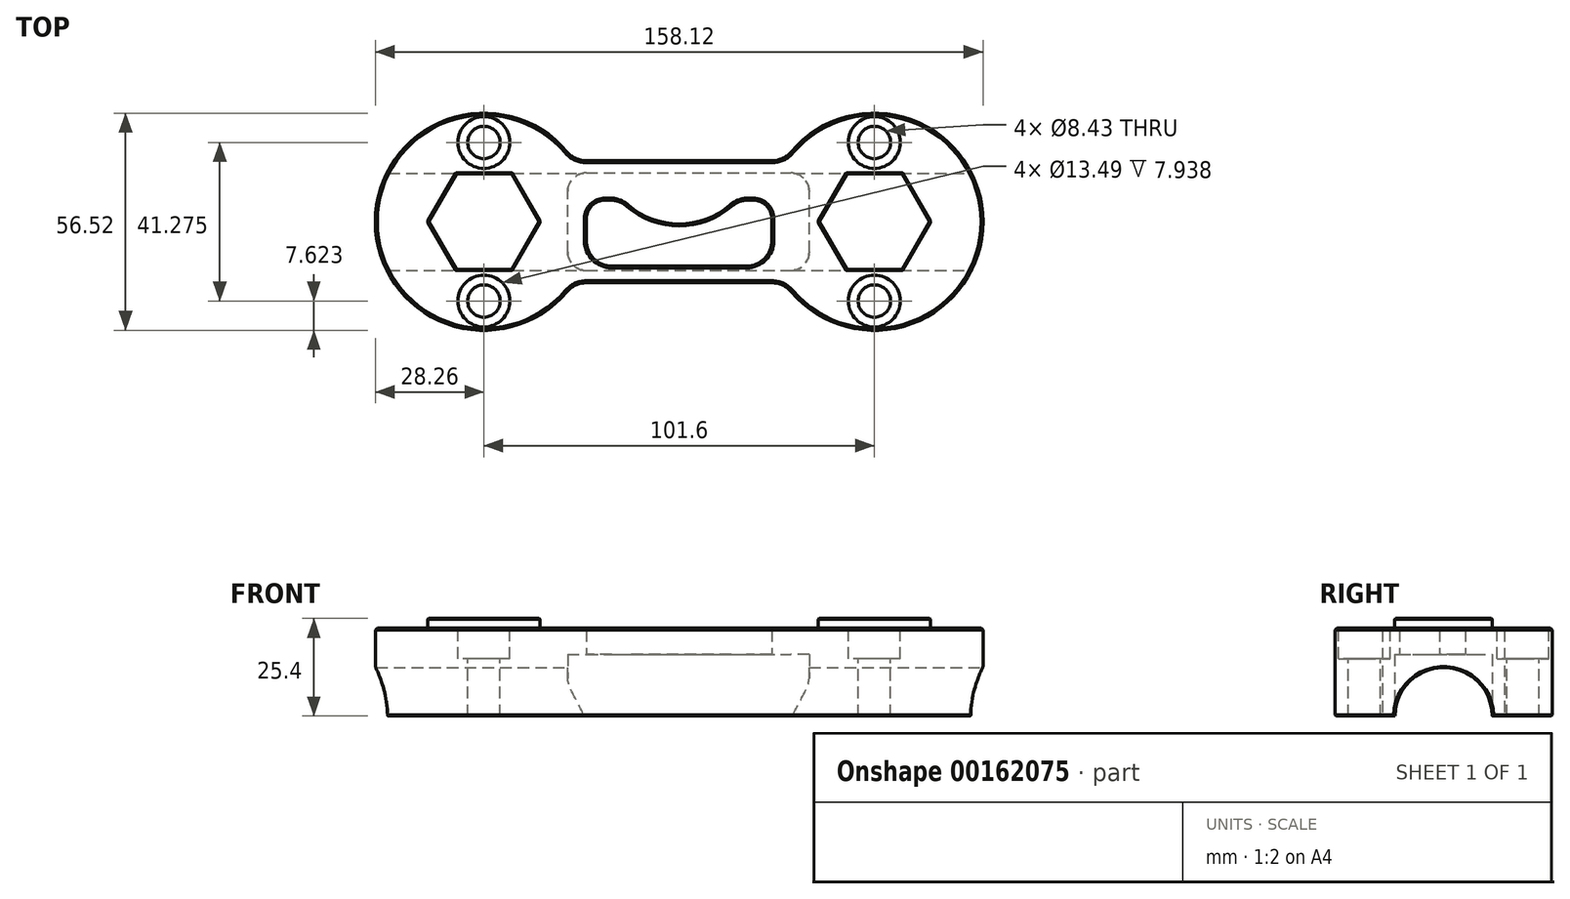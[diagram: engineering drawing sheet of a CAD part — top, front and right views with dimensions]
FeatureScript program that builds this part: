
annotation { "Feature Type Name" : "Feature", "Feature Type Description" : "" }
export const myFeature = defineFeature(function(context is Context, id is Id, definition is map)
    precondition{}
    {
        {
            var Q0;
            Q0=qCreatedBy(makeId("Top.planeOp"),FACE);
            var sketch = newSketch(context, id + "F0", { "sketchPlane" : qUnion([Q0])});
            skPoint(sketch, "E0", {"position": v(-50.8, 0) * mm});
            skPoint(sketch, "E1", {"position": v(50.8, 0) * mm});
            skArc(sketch, "E2", {"start": v(-29.2, 18.22) * mm, "mid": v(-79.06, 0) * mm, "end": v(-29.2, -18.22) * mm});
            skArc(sketch, "E3", {"start": v(29.2, -18.22) * mm, "mid": v(79.06, 0) * mm, "end": v(29.2, 18.22) * mm});
            skLineSegment(sketch, "E4", {"start": v(-24.15, 15.88) * mm, "end": v(24.15, 15.88) * mm});
            skLineSegment(sketch, "E5", {"start": v(-24.15, -15.87) * mm, "end": v(24.15, -15.87) * mm});
            skPoint(sketch, "E6.orphan", {"position": v(-45.55, -15.87) * mm});
            skPoint(sketch, "E7.orphan", {"position": v(-45.55, 15.88) * mm});
            skPoint(sketch, "E8.orphan", {"position": v(44.18, 15.88) * mm});
            skPoint(sketch, "E9.orphan", {"position": v(44.18, -15.87) * mm});
            skPoint(sketch, "E10.visualSharp", {"position": v(-27.42, 15.88) * mm});
            skArc(sketch, "E10.filletArc", {"start": v(-29.2, 18.22) * mm, "mid": v(-26.94, 16.5) * mm, "end": v(-24.15, 15.88) * mm});
            skPoint(sketch, "E11.visualSharp", {"position": v(27.42, 15.88) * mm});
            skArc(sketch, "E11.filletArc", {"start": v(24.15, 15.88) * mm, "mid": v(26.94, 16.5) * mm, "end": v(29.2, 18.22) * mm});
            skPoint(sketch, "E12.visualSharp", {"position": v(-27.42, -15.88) * mm});
            skArc(sketch, "E12.filletArc", {"start": v(-24.15, -15.88) * mm, "mid": v(-26.94, -16.5) * mm, "end": v(-29.2, -18.22) * mm});
            skPoint(sketch, "E13.visualSharp", {"position": v(27.42, -15.87) * mm});
            skArc(sketch, "E13.filletArc", {"start": v(29.2, -18.22) * mm, "mid": v(26.94, -16.5) * mm, "end": v(24.15, -15.88) * mm});
            skSolve(sketch);
        }
        {
            var Q0;
            Q0 = qSketchRegion(id + "F0", true);
            extrude(context, id + "F1", {"entities" : qUnion([Q0]), "depth" : 22.86 * mm});
        }
        {
            var Q0;
            Q0=qCreatedBy(makeId("Right.planeOp"),FACE);
            var sketch = newSketch(context, id + "F2", { "sketchPlane" : qUnion([Q0])});
            skCircle(sketch, "E14", {"center": v(0, 0) * mm, "radius": 12.64 * mm});
            skSolve(sketch);
        }
        {
            var Q0;
            Q0 = qSketchRegion(id + "F2", true);
            extrude(context, id + "F3", {"entities" : qUnion([Q0]), "operationType" : NewBodyOperationType.REMOVE, "endBound" : BoundingType.THROUGH_ALL, "oppositeDirection" : true, "depth" : 25.4 * mm, "hasSecondDirection" : true, "secondDirectionBound" : SecondDirectionBoundingType.THROUGH_ALL, "secondDirectionOppositeDirection" : false, "secondDirectionDepth" : 25.4 * mm});
        }
        {
            var Q0;
            Q0=qCreatedBy(makeId("Top.planeOp"),FACE);
            var sketch = newSketch(context, id + "F4", { "sketchPlane" : qUnion([Q0])});
            skPoint(sketch, "E15", {"position": v(-50.73, 0.06) * mm});
            skPoint(sketch, "E16", {"position": v(50.87, 0.06) * mm});
            skLineSegment(sketch, "E17.bottom", {"start": v(-24.18, -12.7) * mm, "end": v(29.02, -12.7) * mm});
            skLineSegment(sketch, "E17.top", {"start": v(-24.18, 12.7) * mm, "end": v(29.02, 12.7) * mm});
            skLineSegment(sketch, "E17.left", {"start": v(-29, -7.87) * mm, "end": v(-29, 7.87) * mm});
            skLineSegment(sketch, "E17.right", {"start": v(33.84, -7.87) * mm, "end": v(33.84, 7.87) * mm});
            skPoint(sketch, "E18.visualSharp", {"position": v(-29, -12.7) * mm});
            skArc(sketch, "E18.filletArc", {"start": v(-29, -7.87) * mm, "mid": v(-27.6, -11.29) * mm, "end": v(-24.18, -12.7) * mm});
            skPoint(sketch, "E19.visualSharp", {"position": v(-29, 12.7) * mm});
            skArc(sketch, "E19.filletArc", {"start": v(-24.18, 12.7) * mm, "mid": v(-27.6, 11.29) * mm, "end": v(-29, 7.87) * mm});
            skPoint(sketch, "E20.visualSharp", {"position": v(33.84, 12.7) * mm});
            skArc(sketch, "E20.filletArc", {"start": v(33.84, 7.87) * mm, "mid": v(32.43, 11.29) * mm, "end": v(29.02, 12.7) * mm});
            skPoint(sketch, "E21.visualSharp", {"position": v(33.84, -12.7) * mm});
            skArc(sketch, "E21.filletArc", {"start": v(29.02, -12.7) * mm, "mid": v(32.43, -11.29) * mm, "end": v(33.84, -7.87) * mm});
            skSolve(sketch);
        }
        {
            var Q0;
            Q0 = qSketchRegion(id + "F4", true);
            extrude(context, id + "F5", {"entities" : qUnion([Q0]), "operationType" : NewBodyOperationType.REMOVE, "depth" : 16 * mm});
        }
        {
            var Q0;
            Q0=makeQuery(id+"F5.boolean.opBoolean","COPY",FACE,{"derivedFrom":makeQuery(id+"F5.opExtrude","CAP_FACE",FACE,{"disambiguationData":[OSD([sQuery(id+"F4.wireOp",EDGE,"E17.bottom"),sQuery(id+"F4.wireOp",EDGE,"E17.top"),sQuery(id+"F4.wireOp",EDGE,"E17.left"),sQuery(id+"F4.wireOp",EDGE,"E17.right")])],"isStart":false})});
            var sketch = newSketch(context, id + "F6", { "sketchPlane" : qUnion([Q0])});
            skPoint(sketch, "E22.middle", {"position": v(0, 0) * mm});
            skLineSegment(sketch, "E23.bottom", {"start": v(-17.53, 11.52) * mm, "end": v(17.53, 11.52) * mm});
            skLineSegment(sketch, "E23.top", {"start": v(-19.3, -5.63) * mm, "end": v(-17.92, -5.63) * mm});
            skLineSegment(sketch, "E23.left", {"start": v(-24.13, 4.91) * mm, "end": v(-24.13, -0.8) * mm});
            skLineSegment(sketch, "E23.right", {"start": v(24.13, 4.91) * mm, "end": v(24.13, -0.8) * mm});
            skPoint(sketch, "E23.middle", {"position": v(0, 2.94) * mm});
            skPoint(sketch, "E24", {"position": v(-15.24, -5.63) * mm});
            skPoint(sketch, "E25", {"position": v(15.24, -5.63) * mm});
            skArc(sketch, "E26", {"start": v(13.57, -4) * mm, "mid": v(0, 1.1) * mm, "end": v(-13.57, -4) * mm});
            skLineSegment(sketch, "E27.trimOffspring", {"start": v(17.92, -5.63) * mm, "end": v(19.3, -5.63) * mm});
            skPoint(sketch, "E28.visualSharp", {"position": v(-24.13, 11.52) * mm});
            skArc(sketch, "E28.filletArc", {"start": v(-17.53, 11.52) * mm, "mid": v(-22.2, 9.58) * mm, "end": v(-24.13, 4.91) * mm});
            skPoint(sketch, "E29.visualSharp", {"position": v(24.13, 11.52) * mm});
            skArc(sketch, "E29.filletArc", {"start": v(24.13, 4.91) * mm, "mid": v(22.2, 9.58) * mm, "end": v(17.53, 11.52) * mm});
            skPoint(sketch, "E30.visualSharp", {"position": v(-24.13, -5.63) * mm});
            skArc(sketch, "E30.filletArc", {"start": v(-24.13, -0.8) * mm, "mid": v(-22.72, -4.21) * mm, "end": v(-19.3, -5.63) * mm});
            skArc(sketch, "E31.filletArc", {"start": v(-17.92, -5.63) * mm, "mid": v(-15.6, -5.2) * mm, "end": v(-13.57, -4) * mm});
            skPoint(sketch, "E32.visualSharp", {"position": v(24.13, -5.63) * mm});
            skArc(sketch, "E32.filletArc", {"start": v(19.3, -5.63) * mm, "mid": v(22.72, -4.21) * mm, "end": v(24.13, -0.8) * mm});
            skArc(sketch, "E33.filletArc", {"start": v(13.57, -4) * mm, "mid": v(15.6, -5.2) * mm, "end": v(17.92, -5.63) * mm});
            skSolve(sketch);
        }
        {
            var Q0;
            Q0 = qSketchRegion(id + "F6", true);
            extrude(context, id + "F7", {"entities" : qUnion([Q0]), "operationType" : NewBodyOperationType.REMOVE, "oppositeDirection" : true, "depth" : 25.4 * mm});
        }
        {
            var Q0;
            Q0=makeQuery(id+"F1.opExtrude","CAP_FACE",FACE,{"disambiguationData":[OSD([sQuery(id+"F0.wireOp",EDGE,"E2"),sQuery(id+"F0.wireOp",EDGE,"E3"),sQuery(id+"F0.wireOp",EDGE,"E4"),sQuery(id+"F0.wireOp",EDGE,"E5"),sQuery(id+"F0.wireOp",EDGE,"E10.filletArc"),sQuery(id+"F0.wireOp",EDGE,"E11.filletArc"),sQuery(id+"F0.wireOp",EDGE,"E12.filletArc"),sQuery(id+"F0.wireOp",EDGE,"E13.filletArc")])],"isStart":false});
            var sketch = newSketch(context, id + "F8", { "sketchPlane" : qUnion([Q0])});
            skCircle(sketch, "E34", {"center": v(-50.8, 0) * mm, "radius": 12.7 * mm});
            skCircle(sketch, "E35", {"center": v(50.8, 0) * mm, "radius": 12.7 * mm});
            skCircle(sketch, "E36.cCircle", {"center": v(-50.8, 0) * mm, "radius": 12.7 * mm, "construction": true});
            skLineSegment(sketch, "E36.0", {"start": v(-58.13, 12.7) * mm, "end": v(-43.47, 12.7) * mm});
            skLineSegment(sketch, "E36.1", {"start": v(-43.47, 12.7) * mm, "end": v(-36.14, 0) * mm});
            skLineSegment(sketch, "E36.2", {"start": v(-36.14, 0) * mm, "end": v(-43.47, -12.7) * mm});
            skLineSegment(sketch, "E36.3", {"start": v(-43.47, -12.7) * mm, "end": v(-58.13, -12.7) * mm});
            skLineSegment(sketch, "E36.4", {"start": v(-58.13, -12.7) * mm, "end": v(-65.46, 0) * mm});
            skLineSegment(sketch, "E36.5", {"start": v(-65.46, 0) * mm, "end": v(-58.13, 12.7) * mm});
            skPoint(sketch, "E36.0.midPoint", {"position": v(-50.8, 12.7) * mm});
            skCircle(sketch, "E37.cCircle", {"center": v(50.8, 0) * mm, "radius": 12.7 * mm, "construction": true});
            skLineSegment(sketch, "E37.0", {"start": v(43.47, 12.7) * mm, "end": v(58.13, 12.7) * mm});
            skLineSegment(sketch, "E37.1", {"start": v(58.13, 12.7) * mm, "end": v(65.46, 0) * mm});
            skLineSegment(sketch, "E37.2", {"start": v(65.46, 0) * mm, "end": v(58.13, -12.7) * mm});
            skLineSegment(sketch, "E37.3", {"start": v(58.13, -12.7) * mm, "end": v(43.47, -12.7) * mm});
            skLineSegment(sketch, "E37.4", {"start": v(43.47, -12.7) * mm, "end": v(36.14, 0) * mm});
            skLineSegment(sketch, "E37.5", {"start": v(36.14, 0) * mm, "end": v(43.47, 12.7) * mm});
            skPoint(sketch, "E37.0.midPoint", {"position": v(50.8, 12.7) * mm});
            skSolve(sketch);
        }
        {
            var Q0;
            Q0 = qSketchRegion(id + "F8", true);
            extrude(context, id + "F9", {"entities" : qUnion([Q0]), "operationType" : NewBodyOperationType.ADD, "depth" : 2.54 * mm});
        }
        {
            var Q0;
            Q0=makeQuery(id+"F1.opExtrude","CAP_FACE",FACE,{"disambiguationData":[OSD([sQuery(id+"F0.wireOp",EDGE,"E2"),sQuery(id+"F0.wireOp",EDGE,"E3"),sQuery(id+"F0.wireOp",EDGE,"E4"),sQuery(id+"F0.wireOp",EDGE,"E5"),sQuery(id+"F0.wireOp",EDGE,"E10.filletArc"),sQuery(id+"F0.wireOp",EDGE,"E11.filletArc"),sQuery(id+"F0.wireOp",EDGE,"E12.filletArc"),sQuery(id+"F0.wireOp",EDGE,"E13.filletArc")])],"isStart":false});
            var sketch = newSketch(context, id + "F10", { "sketchPlane" : qUnion([Q0])});
            skPoint(sketch, "E38.startSnap0", {"position": v(-50.8, 12.7) * mm});
            skPoint(sketch, "E39.startSnap0", {"position": v(50.8, 12.7) * mm});
            skPoint(sketch, "E39.endSnap0", {"position": v(50.8, -12.7) * mm});
            skPoint(sketch, "E40", {"position": v(-50.8, 20.64) * mm});
            skPoint(sketch, "E41", {"position": v(-50.8, -20.64) * mm});
            skPoint(sketch, "E42", {"position": v(50.8, 20.64) * mm});
            skPoint(sketch, "E43", {"position": v(50.8, -20.64) * mm});
            skSolve(sketch);
        }
        {
            var Q0;
            Q0=sQuery(id+"F10.wireOp",VERTEX,"E40");
            var Q1;
            Q1=sQuery(id+"F10.wireOp",VERTEX,"E41");
            var Q2;
            Q2=sQuery(id+"F10.wireOp",VERTEX,"E42");
            var Q3;
            Q3=sQuery(id+"F10.wireOp",VERTEX,"E43");
            var Q4;
            Q4=makeQuery(id+"F1.opExtrude","SWEPT_BODY",BODY,{"disambiguationData":[OSD([sQuery(id+"F0.wireOp",EDGE,"E2"),sQuery(id+"F0.wireOp",EDGE,"E3"),sQuery(id+"F0.wireOp",EDGE,"E4"),sQuery(id+"F0.wireOp",EDGE,"E5"),sQuery(id+"F0.wireOp",EDGE,"E10.filletArc"),sQuery(id+"F0.wireOp",EDGE,"E11.filletArc"),sQuery(id+"F0.wireOp",EDGE,"E12.filletArc"),sQuery(id+"F0.wireOp",EDGE,"E13.filletArc")])]});
            hole(context, id + "F11", {"style" : HoleStyle.C_BORE, "endStyle" : HoleEndStyle.THROUGH, "standardTappedOrClearance" : lookupTablePath({ "standard" : "ANSI", "fit" : "Normal (ASME)", "size" : "5/16", "type" : "Clearance" }), "standardBlindInLast" : lookupTablePath({ "fit" : "Free", "standard" : "ANSI", "size" : "5/16", "type" : "Clearance" }), "holeDiameter" : 8.43 * mm, "cBoreDiameter" : 13.5 * mm, "cBoreDepth" : 7.94 * mm, "locations" : qUnion([Q0, Q1, Q2, Q3]), "scope" : qUnion([Q4]), "isTappedThrough" : true});
        }
        {
            var Q0;
            Q0=makeQuery(id+"F11.hole-0.boolean.opBoolean","COPY",EDGE,{"derivedFrom":makeQuery(id+"F11.hole-0.opRevolve","SWEPT_EDGE",EDGE,{"disambiguationData":[OSD([sQuery(id+"F11.hole-0.sketch.wireOp",EDGE,"cbore_start_line_2"),sQuery(id+"F11.hole-0.sketch.wireOp",EDGE,"cbore_start_line_3")])]})});
            var Q1;
            Q1=makeQuery(id+"F11.hole-1.boolean.opBoolean","COPY",EDGE,{"derivedFrom":makeQuery(id+"F11.hole-1.opRevolve","SWEPT_EDGE",EDGE,{"disambiguationData":[OSD([sQuery(id+"F11.hole-1.sketch.wireOp",EDGE,"cbore_start_line_2"),sQuery(id+"F11.hole-1.sketch.wireOp",EDGE,"cbore_start_line_3")])]})});
            var Q2;
            Q2=makeQuery(id+"F11.hole-3.boolean.opBoolean","COPY",EDGE,{"derivedFrom":makeQuery(id+"F11.hole-3.opRevolve","SWEPT_EDGE",EDGE,{"disambiguationData":[OSD([sQuery(id+"F11.hole-3.sketch.wireOp",EDGE,"cbore_start_line_2"),sQuery(id+"F11.hole-3.sketch.wireOp",EDGE,"cbore_start_line_3")])]})});
            var Q3;
            Q3=makeQuery(id+"F11.hole-2.boolean.opBoolean","COPY",EDGE,{"derivedFrom":makeQuery(id+"F11.hole-2.opRevolve","SWEPT_EDGE",EDGE,{"disambiguationData":[OSD([sQuery(id+"F11.hole-2.sketch.wireOp",EDGE,"cbore_start_line_2"),sQuery(id+"F11.hole-2.sketch.wireOp",EDGE,"cbore_start_line_3")])]})});
            var Q4;
            Q4=makeQuery(id+"F9.opExtrude","CAP_FACE",FACE,{"disambiguationData":[OSD([sQuery(id+"F8.wireOp",EDGE,"E36.0"),sQuery(id+"F8.wireOp",EDGE,"E36.1"),sQuery(id+"F8.wireOp",EDGE,"E36.2"),sQuery(id+"F8.wireOp",EDGE,"E36.3"),sQuery(id+"F8.wireOp",EDGE,"E36.4"),sQuery(id+"F8.wireOp",EDGE,"E36.5")])],"isStart":false});
            var Q5;
            Q5=makeQuery(id+"F9.opExtrude","CAP_FACE",FACE,{"disambiguationData":[OSD([sQuery(id+"F8.wireOp",EDGE,"E37.0"),sQuery(id+"F8.wireOp",EDGE,"E37.1"),sQuery(id+"F8.wireOp",EDGE,"E37.2"),sQuery(id+"F8.wireOp",EDGE,"E37.3"),sQuery(id+"F8.wireOp",EDGE,"E37.4"),sQuery(id+"F8.wireOp",EDGE,"E37.5")])],"isStart":false});
            chamfer(context, id + "F12", {"entities" : qUnion([Q0, Q1, Q2, Q3, Q4, Q5]), "width" : 0.25 * mm, "tangentPropagation" : true});
        }
        {
            var Q0;
            Q0=makeQuery(id+"F1.opExtrude","CAP_EDGE",EDGE,{"disambiguationData":[OSD([sQuery(id+"F0.wireOp",EDGE,"E12.filletArc")])],"isStart":false});
            var Q1;
            Q1=makeQuery(id+"F1.opExtrude","CAP_EDGE",EDGE,{"disambiguationData":[OSD([sQuery(id+"F0.wireOp",EDGE,"E2")])],"isStart":false});
            var Q2;
            Q2=makeQuery(id+"F7.boolean.opBoolean","INTERSECT",EDGE,{"derivedFrom":[makeQuery(id+"F1.opExtrude","CAP_FACE",FACE,{"disambiguationData":[OSD([sQuery(id+"F0.wireOp",EDGE,"E2"),sQuery(id+"F0.wireOp",EDGE,"E3"),sQuery(id+"F0.wireOp",EDGE,"E4"),sQuery(id+"F0.wireOp",EDGE,"E5"),sQuery(id+"F0.wireOp",EDGE,"E10.filletArc"),sQuery(id+"F0.wireOp",EDGE,"E11.filletArc"),sQuery(id+"F0.wireOp",EDGE,"E12.filletArc"),sQuery(id+"F0.wireOp",EDGE,"E13.filletArc")])],"isStart":false}),makeQuery(id+"F7.opExtrude","SWEPT_FACE",FACE,{"disambiguationData":[OSD([sQuery(id+"F6.wireOp",EDGE,"E23.left")])]})]});
            var Q3;
            Q3=makeQuery(id+"F7.boolean.opBoolean","INTERSECT",EDGE,{"derivedFrom":[makeQuery(id+"F1.opExtrude","CAP_FACE",FACE,{"disambiguationData":[OSD([sQuery(id+"F0.wireOp",EDGE,"E2"),sQuery(id+"F0.wireOp",EDGE,"E3"),sQuery(id+"F0.wireOp",EDGE,"E4"),sQuery(id+"F0.wireOp",EDGE,"E5"),sQuery(id+"F0.wireOp",EDGE,"E10.filletArc"),sQuery(id+"F0.wireOp",EDGE,"E11.filletArc"),sQuery(id+"F0.wireOp",EDGE,"E12.filletArc"),sQuery(id+"F0.wireOp",EDGE,"E13.filletArc")])],"isStart":false}),makeQuery(id+"F7.opExtrude","SWEPT_FACE",FACE,{"disambiguationData":[OSD([sQuery(id+"F6.wireOp",EDGE,"E30.filletArc")])]})]});
            chamfer(context, id + "F13", {"entities" : qUnion([Q0, Q1, Q2, Q3]), "width" : 0.5 * mm, "tangentPropagation" : true});
        }
        {
            var Q0;
            Q0=makeQuery(id+"F9.opExtrude","SWEPT_EDGE",EDGE,{"disambiguationData":[OSD([sQuery(id+"F8.wireOp",EDGE,"E36.2"),sQuery(id+"F8.wireOp",EDGE,"E36.3")])]});
            var Q1;
            Q1=makeQuery(id+"F9.opExtrude","SWEPT_EDGE",EDGE,{"disambiguationData":[OSD([sQuery(id+"F8.wireOp",EDGE,"E36.1"),sQuery(id+"F8.wireOp",EDGE,"E36.2")])]});
            var Q2;
            Q2=makeQuery(id+"F9.opExtrude","SWEPT_EDGE",EDGE,{"disambiguationData":[OSD([sQuery(id+"F8.wireOp",EDGE,"E36.3"),sQuery(id+"F8.wireOp",EDGE,"E36.4")])]});
            var Q3;
            Q3=makeQuery(id+"F9.opExtrude","SWEPT_EDGE",EDGE,{"disambiguationData":[OSD([sQuery(id+"F8.wireOp",EDGE,"E36.4"),sQuery(id+"F8.wireOp",EDGE,"E36.5")])]});
            var Q4;
            Q4=makeQuery(id+"F9.opExtrude","SWEPT_EDGE",EDGE,{"disambiguationData":[OSD([sQuery(id+"F8.wireOp",EDGE,"E36.0"),sQuery(id+"F8.wireOp",EDGE,"E36.5")])]});
            var Q5;
            Q5=makeQuery(id+"F9.opExtrude","SWEPT_EDGE",EDGE,{"disambiguationData":[OSD([sQuery(id+"F8.wireOp",EDGE,"E36.0"),sQuery(id+"F8.wireOp",EDGE,"E36.1")])]});
            var Q6;
            Q6=makeQuery(id+"F9.opExtrude","SWEPT_EDGE",EDGE,{"disambiguationData":[OSD([sQuery(id+"F8.wireOp",EDGE,"E37.2"),sQuery(id+"F8.wireOp",EDGE,"E37.3")])]});
            var Q7;
            Q7=makeQuery(id+"F9.opExtrude","SWEPT_EDGE",EDGE,{"disambiguationData":[OSD([sQuery(id+"F8.wireOp",EDGE,"E37.1"),sQuery(id+"F8.wireOp",EDGE,"E37.2")])]});
            var Q8;
            Q8=makeQuery(id+"F9.opExtrude","SWEPT_EDGE",EDGE,{"disambiguationData":[OSD([sQuery(id+"F8.wireOp",EDGE,"E37.3"),sQuery(id+"F8.wireOp",EDGE,"E37.4")])]});
            var Q9;
            Q9=makeQuery(id+"F9.opExtrude","SWEPT_EDGE",EDGE,{"disambiguationData":[OSD([sQuery(id+"F8.wireOp",EDGE,"E37.0"),sQuery(id+"F8.wireOp",EDGE,"E37.1")])]});
            var Q10;
            Q10=makeQuery(id+"F9.opExtrude","SWEPT_EDGE",EDGE,{"disambiguationData":[OSD([sQuery(id+"F8.wireOp",EDGE,"E37.0"),sQuery(id+"F8.wireOp",EDGE,"E37.5")])]});
            var Q11;
            Q11=makeQuery(id+"F9.opExtrude","SWEPT_EDGE",EDGE,{"disambiguationData":[OSD([sQuery(id+"F8.wireOp",EDGE,"E37.4"),sQuery(id+"F8.wireOp",EDGE,"E37.5")])]});
            fillet(context, id + "F14", {"entities" : qUnion([Q0, Q1, Q2, Q3, Q4, Q5, Q6, Q7, Q8, Q9, Q10, Q11]), "radius" : 0.25 * mm, "tangentPropagation" : true, "allowEdgeOverflow" : false});
        }
        {
            var Q0;
            {var subQ0=sQuery(id+"F0.wireOp",EDGE,"E2");var subQ1=sQuery(id+"F0.wireOp",EDGE,"E10.filletArc");Q0=makeQuery(id+"F3.boolean.opBoolean","SPLIT",EDGE,{"disambiguationData":[TD([makeQuery(id+"F1.opExtrude","SWEPT_FACE",FACE,{"disambiguationData":[OSD([subQ1])]})])],"derivedFrom":makeQuery(id+"F1.opExtrude","CAP_EDGE",EDGE,{"disambiguationData":[OSD([subQ0])],"isStart":true})});}
            var Q1;
            Q1=makeQuery(id+"F1.opExtrude","CAP_EDGE",EDGE,{"disambiguationData":[OSD([sQuery(id+"F0.wireOp",EDGE,"E10.filletArc")])],"isStart":true});
            var Q2;
            {var subQ0=sQuery(id+"F0.wireOp",EDGE,"E13.filletArc");var subQ1=sQuery(id+"F0.wireOp",EDGE,"E3");Q2=makeQuery(id+"F3.boolean.opBoolean","SPLIT",EDGE,{"disambiguationData":[TD([makeQuery(id+"F1.opExtrude","SWEPT_FACE",FACE,{"disambiguationData":[OSD([subQ0])]})])],"derivedFrom":makeQuery(id+"F1.opExtrude","CAP_EDGE",EDGE,{"disambiguationData":[OSD([subQ1])],"isStart":true})});}
            chamfer(context, id + "F15", {"entities" : qUnion([Q0, Q1, Q2]), "width" : 0.25 * mm, "tangentPropagation" : true});
        }
        {
            var Q0;
            Q0=makeQuery(id+"F3.boolean.opBoolean","INTERSECT",EDGE,{"derivedFrom":[makeQuery(id+"F1.opExtrude","SWEPT_FACE",FACE,{"disambiguationData":[OSD([sQuery(id+"F0.wireOp",EDGE,"E3")])]}),makeQuery(id+"F3.opExtrude","SWEPT_FACE",FACE,{"disambiguationData":[OSD([sQuery(id+"F2.wireOp",EDGE,"E14")])]})]});
            var Q1;
            Q1=makeQuery(id+"F3.boolean.opBoolean","INTERSECT",EDGE,{"derivedFrom":[makeQuery(id+"F1.opExtrude","SWEPT_FACE",FACE,{"disambiguationData":[OSD([sQuery(id+"F0.wireOp",EDGE,"E2")])]}),makeQuery(id+"F3.opExtrude","SWEPT_FACE",FACE,{"disambiguationData":[OSD([sQuery(id+"F2.wireOp",EDGE,"E14")])]})]});
            chamfer(context, id + "F16", {"entities" : qUnion([Q0, Q1]), "width" : 0.25 * mm, "tangentPropagation" : true});
        }
    });
